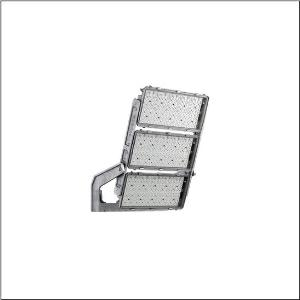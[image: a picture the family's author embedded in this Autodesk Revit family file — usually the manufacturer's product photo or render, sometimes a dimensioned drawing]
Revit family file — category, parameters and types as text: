
# Revit family: floodlight_fl_11_maxi_pro_remote___pl64_5xa779424v01aa_c523
name_source: partatom
category: Lighting Fixtures
units: mm (PartAtom-declared; Revit-internal decimal feet)

## family parameters
Cut with Voids When Loaded = No
Host = Face
Light Source = No
Part Type = Normal
Room Calculation Point = No
Round Connector Dimension = Use Diameter
Shared = No

## types (1)
- --- (1 x LED, 168380 lm, 1539.3 W, 5700K)
    Apparent Load = 1539 VA
    CIE Flux Codes = 28 79 98 100 100
    Color Rendering = 90
    Color Temperature = 5700K
    Default Elevation = 1800 mm
    Description = Floodlight FL 11  maxi  pro Remote floodlight; light control with lens of PMMA; cover panel of toughened safety glass, transparent; light distribution: PL64, asymmetric direct distribution, LEDcolour temperature: 5700K, rated luminous flux: 168.380lm, colour rendering: CRI > 90, light colour: 957; luminous efficacy: 109lm/W; brightness control: DALI 2 (1 DALI address); with terminal, 8-pole, max. 2.5mm², mains connection: 220..240V/380..400V AC, 50/60Hz, surge voltage resistance: line to ground: 10kV, ECG replaceable separately, no afterglow with DALI off / DMX off command, LED unit replaceable without ESD environment, dustproof LED module, dimming range 10..100%; 1539W floodlight with 3x LED unit of diecast aluminium, coated grey; length: 1.003mm / width: 651mm / height: 338mm; mounting bracket, of diecast aluminium, uncoated, natural, equipment: Power, protection rating (complete): IP66; insulation class (complete): insulation class I (protective earthing); certification: CE; ball protection: ball impact resistance with accessories, impact resistance: IK07; only for outdoor installations, rated ambient temperature 10°C, permissible operating ambient temperature: -40..+30°C, permissible storage temperature: -40..+85°C; packaging unit: 1 piece

Light Distribution: PL64
    Height = 320 mm
    Lamp = 1 x LED
    Lamp Light Flux = 168380 lm
    Lamp Power = 1539.3 W
    Lamp count = 1
    Length = 1002 mm
    Luminous efficacy = 109 lm/W
    Manufacturer = Siteco
    ModVariant = No
    Model = 5XA779424V01AA
    Mounting Place = Ceiling
    Mounting Type = Surface mounted
    Number of Poles = 1
    OnlyDefault = Yes
    Power Factor = 1
    Product Name = Floodlight FL 11 maxi pro Remote | PL64
    Product group = floodlight | ceiling mounted
    ProductGroupID = 303
    Protection Class = Protection class I
    Protection Degree = IP 66
    RLX_Detail_Level = 1
    RLX_Emergency_Light_Flux = 0 lm
    RLX_Emergency_Type = 0
    RLX_Emergency_Type_DB = No
    RlxData = <blob elided: 52509 chars, md5=55ccea31>
    Socket = socket
    Standby Power = 0 W
    System Light Flux = 168380 lm
    System Power = 1539 W
    Type Comments = factory setting: luminous flux: 100 % | dim-lin: 254 | 1080 mA
    Type Image = l_1006784.jpg
    URL = http://relux.com
    VarID = @adj_050723
    Voltage = 0 V
    Weight = 0.00 kg
    Width = 655 mm

## geometry (parser evidence)
native form markers: Blend x4, Sweep x12
no freeform markers — native parametric forms only
